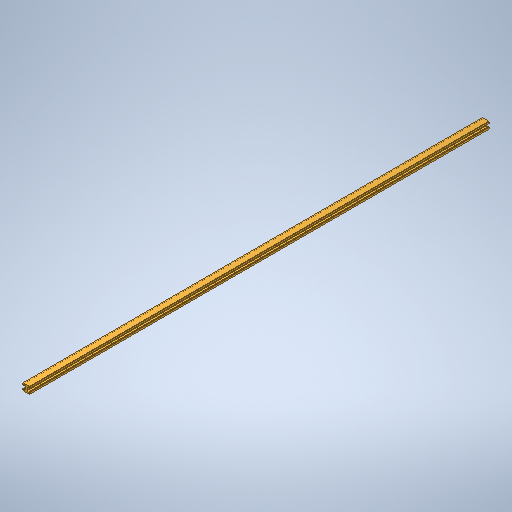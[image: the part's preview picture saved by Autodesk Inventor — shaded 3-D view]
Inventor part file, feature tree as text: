
AUTODESK INVENTOR PART (.ipt)
format: ipt  version: 2025.2 (Build 292293000, 293)  size: 323,584 bytes
history: native  units: mm
features: mirror x2, other x1, extrude x1, sketch x1
ambient origin geometry x8: Origin, YZ Plane, XZ Plane, XY Plane, X Axis, Y Axis, Z Axis, Center Point
bodies: Body1 (feature_tree)
feature tree (5):
  other  "Sólido1"
  extrude  "Extrusão1"  Depth=6.2mm
  mirror  "Espelhar1"
  mirror  "Espelhar2"
  sketch  "Esboço1"  dims[d0=15.0mm d1=6.2mm d2=7.5mm d4=2.0mm d5=6.0mm d7=3.1mm d8=1000.0mm d9=0.0mm d10=0.5mm d11=0.5mm d12=0.2mm d13=0.5mm]
